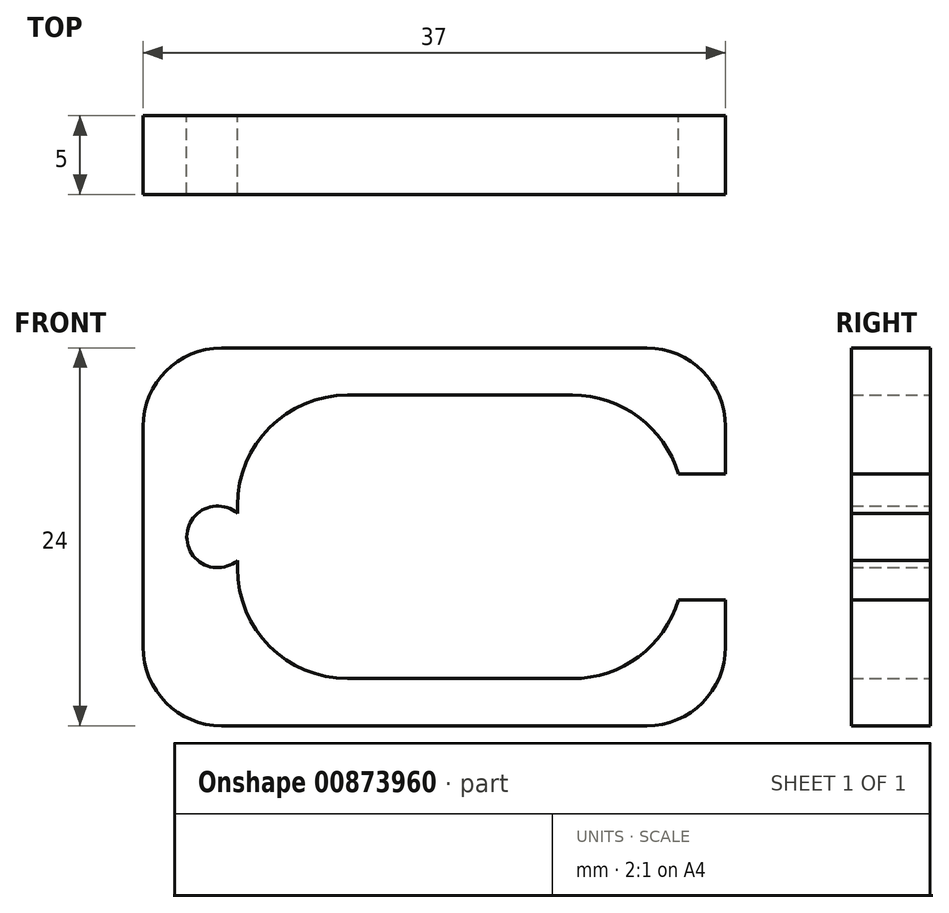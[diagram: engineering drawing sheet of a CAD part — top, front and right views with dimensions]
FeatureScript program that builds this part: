
annotation { "Feature Type Name" : "Feature", "Feature Type Description" : "" }
export const myFeature = defineFeature(function(context is Context, id is Id, definition is map)
    precondition{}
    {
        {
            var Q0;
            Q0=qCreatedBy(makeId("Front.planeOp"),FACE);
            var sketch = newSketch(context, id + "F0", { "sketchPlane" : qUnion([Q0])});
            skLineSegment(sketch, "E0.bottom", {"start": v(-18.5, 12) * mm, "end": v(18.5, 12) * mm});
            skLineSegment(sketch, "E0.top", {"start": v(-18.5, -12) * mm, "end": v(18.5, -12) * mm});
            skLineSegment(sketch, "E0.left", {"start": v(-18.5, 12) * mm, "end": v(-18.5, -12) * mm});
            skPoint(sketch, "E0.middle", {"position": v(0, 0) * mm});
            skLineSegment(sketch, "E1", {"start": v(18.5, 12) * mm, "end": v(18.5, 4) * mm});
            skLineSegment(sketch, "E2", {"start": v(15.5, 4) * mm, "end": v(15.5, 9) * mm});
            skLineSegment(sketch, "E3", {"start": v(15.5, 9) * mm, "end": v(-12.5, 9) * mm});
            skLineSegment(sketch, "E4", {"start": v(-12.5, -9) * mm, "end": v(15.5, -9) * mm});
            skLineSegment(sketch, "E5", {"start": v(15.5, -9) * mm, "end": v(15.5, -4) * mm});
            skLineSegment(sketch, "E6", {"start": v(18.5, -4) * mm, "end": v(18.5, -12) * mm});
            skLineSegment(sketch, "E7", {"start": v(-12.5, 9) * mm, "end": v(-12.5, 1.5) * mm});
            skLineSegment(sketch, "E8", {"start": v(-12.5, -9) * mm, "end": v(-12.5, -1.5) * mm});
            skArc(sketch, "E9", {"start": v(-12.5, 1.5) * mm, "mid": v(-15.71, 0) * mm, "end": v(-12.5, -1.5) * mm});
            skLineSegment(sketch, "E10", {"start": v(18.5, 4) * mm, "end": v(15.5, 4) * mm});
            skLineSegment(sketch, "E11", {"start": v(18.5, -4) * mm, "end": v(15.5, -4) * mm});
            skSolve(sketch);
        }
        {
            var Q0;
            Q0=makeQuery(id+"F0.imprint","IMPRINT",FACE,{"disambiguationData":[TD([[makeQuery(id+"F0.imprint","IMPRINT",EDGE,{"derivedFrom":sQuery(id+"F0.wireOp",EDGE,"E0.bottom")}),-1.0]])]});
            extrude(context, id + "F1", {"entities" : qUnion([Q0]), "endBound" : BoundingType.SYMMETRIC, "depth" : 5 * mm, "offsetDistance" : 25 * mm});
        }
        {
            var Q0;
            Q0=makeQuery(id+"F1.opExtrude","SWEPT_EDGE",EDGE,{"disambiguationData":[OSD([sQuery(id+"F0.wireOp",EDGE,"E0.bottom"),sQuery(id+"F0.wireOp",EDGE,"E0.left")])]});
            var Q1;
            Q1=makeQuery(id+"F1.opExtrude","SWEPT_EDGE",EDGE,{"disambiguationData":[OSD([sQuery(id+"F0.wireOp",EDGE,"E0.bottom"),sQuery(id+"F0.wireOp",EDGE,"E1")])]});
            var Q2;
            Q2=makeQuery(id+"F1.opExtrude","SWEPT_EDGE",EDGE,{"disambiguationData":[OSD([sQuery(id+"F0.wireOp",EDGE,"E0.top"),sQuery(id+"F0.wireOp",EDGE,"E6")])]});
            var Q3;
            Q3=makeQuery(id+"F1.opExtrude","SWEPT_EDGE",EDGE,{"disambiguationData":[OSD([sQuery(id+"F0.wireOp",EDGE,"E0.top"),sQuery(id+"F0.wireOp",EDGE,"E0.left")])]});
            fillet(context, id + "F2", {"entities" : qUnion([Q0, Q1, Q2, Q3]), "radius" : 5 * mm, "tangentPropagation" : true, "allowEdgeOverflow" : false});
        }
        {
            var Q0;
            Q0=makeQuery(id+"F1.opExtrude","SWEPT_EDGE",EDGE,{"disambiguationData":[OSD([sQuery(id+"F0.wireOp",EDGE,"E2"),sQuery(id+"F0.wireOp",EDGE,"E3")])]});
            var Q1;
            Q1=makeQuery(id+"F1.opExtrude","SWEPT_EDGE",EDGE,{"disambiguationData":[OSD([sQuery(id+"F0.wireOp",EDGE,"E4"),sQuery(id+"F0.wireOp",EDGE,"E5")])]});
            var Q2;
            Q2=makeQuery(id+"F1.opExtrude","SWEPT_EDGE",EDGE,{"disambiguationData":[OSD([sQuery(id+"F0.wireOp",EDGE,"E4"),sQuery(id+"F0.wireOp",EDGE,"E8")])]});
            var Q3;
            Q3=makeQuery(id+"F1.opExtrude","SWEPT_EDGE",EDGE,{"disambiguationData":[OSD([sQuery(id+"F0.wireOp",EDGE,"E3"),sQuery(id+"F0.wireOp",EDGE,"E7")])]});
            fillet(context, id + "F3", {"entities" : qUnion([Q0, Q1, Q2, Q3]), "radius" : 7 * mm, "tangentPropagation" : true, "allowEdgeOverflow" : false});
        }
    });
